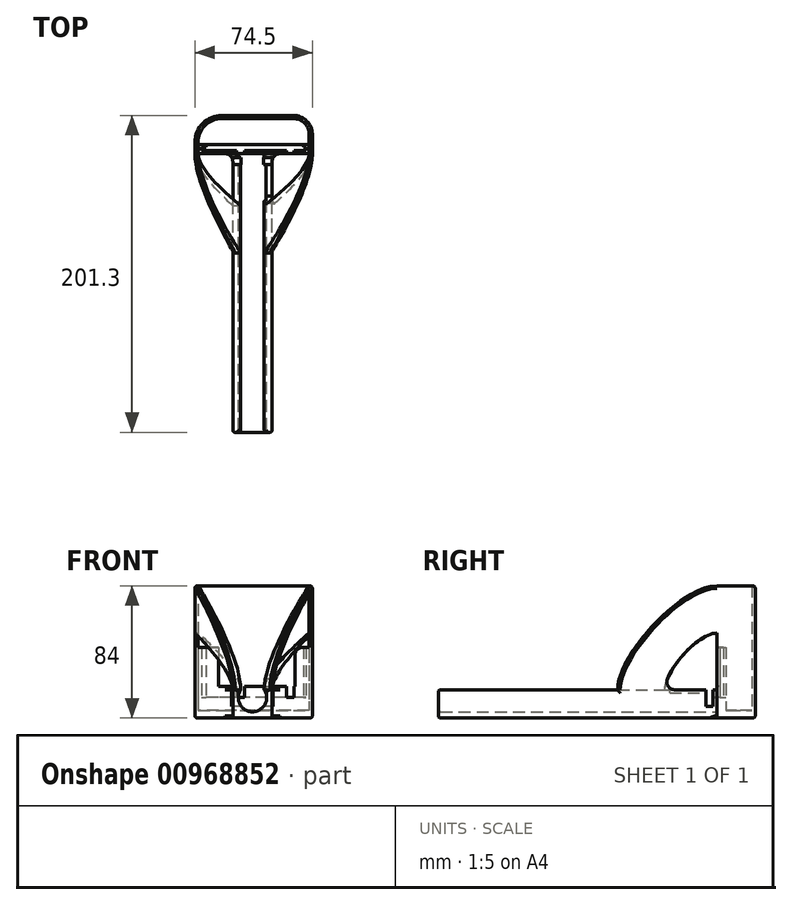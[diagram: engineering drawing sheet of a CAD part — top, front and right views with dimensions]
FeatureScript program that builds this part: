
annotation { "Feature Type Name" : "Feature", "Feature Type Description" : "" }
export const myFeature = defineFeature(function(context is Context, id is Id, definition is map)
    precondition{}
    {
        {
            var Q0;
            Q0=qCreatedBy(makeId("Top.planeOp"),FACE);
            var sketch = newSketch(context, id + "F0", { "sketchPlane" : qUnion([Q0])});
            skLineSegment(sketch, "E0.bottom", {"start": v(0, -2.2) * mm, "end": v(66.5, -2.2) * mm, "construction": true});
            skLineSegment(sketch, "E0.top", {"start": v(0, 0) * mm, "end": v(66.5, 0) * mm, "construction": true});
            skLineSegment(sketch, "E0.left", {"start": v(0, -2.2) * mm, "end": v(0, 0) * mm, "construction": true});
            skLineSegment(sketch, "E0.right", {"start": v(66.5, -2.2) * mm, "end": v(66.5, 0) * mm, "construction": true});
            skLineSegment(sketch, "E1", {"start": v(3, 0) * mm, "end": v(3, 1.6) * mm});
            skLineSegment(sketch, "E2", {"start": v(3, 1.6) * mm, "end": v(-2, 1.6) * mm});
            skLineSegment(sketch, "E3", {"start": v(-2, 1.6) * mm, "end": v(-2, -4.2) * mm});
            skLineSegment(sketch, "E4", {"start": v(-2, -4.2) * mm, "end": v(68.5, -4.2) * mm});
            skLineSegment(sketch, "E5", {"start": v(68.5, -4.2) * mm, "end": v(68.5, 1.6) * mm});
            skLineSegment(sketch, "E6", {"start": v(68.5, 1.6) * mm, "end": v(65, 1.6) * mm});
            skLineSegment(sketch, "E7", {"start": v(65, 1.6) * mm, "end": v(65, 0) * mm});
            skLineSegment(sketch, "E8", {"start": v(65, 0) * mm, "end": v(66.5, 0) * mm});
            skLineSegment(sketch, "E9", {"start": v(66.5, -2.2) * mm, "end": v(0, -2.2) * mm});
            skLineSegment(sketch, "E10", {"start": v(0, -2.2) * mm, "end": v(0, 0) * mm});
            skLineSegment(sketch, "E11", {"start": v(0, 0) * mm, "end": v(3, 0) * mm});
            skLineSegment(sketch, "E12", {"start": v(66.5, 0) * mm, "end": v(66.5, -2.2) * mm});
            skSolve(sketch);
        }
        {
            var Q0;
            Q0=makeQuery(id+"F0.imprint","IMPRINT",FACE,{"disambiguationData":[TD([[makeQuery(id+"F0.imprint","IMPRINT",EDGE,{"derivedFrom":sQuery(id+"F0.wireOp",EDGE,"E1")}),1.0]])]});
            extrude(context, id + "F1", {"entities" : qUnion([Q0]), "depth" : 45 * mm, "offsetDistance" : 25 * mm});
        }
        {
            var Q0;
            Q0=makeQuery(id+"F1.opExtrude","SWEPT_FACE",FACE,{"disambiguationData":[OSD([sQuery(id+"F0.wireOp",EDGE,"E4")])]});
            var sketch = newSketch(context, id + "F2", { "sketchPlane" : qUnion([Q0])});
            skLineSegment(sketch, "E13.0.0", {"start": v(-2, 0) * mm, "end": v(68.5, 0) * mm});
            skLineSegment(sketch, "E13.0.1", {"start": v(68.5, 0) * mm, "end": v(68.5, 45) * mm});
            skLineSegment(sketch, "E13.0.2", {"start": v(68.5, 45) * mm, "end": v(-2, 45) * mm});
            skLineSegment(sketch, "E13.0.3", {"start": v(-2, 45) * mm, "end": v(-2, 0) * mm});
            skLineSegment(sketch, "E14.0.1", {"start": v(0, 0) * mm, "end": v(0, 45) * mm});
            skLineSegment(sketch, "E14.0.3", {"start": v(0, 45) * mm, "end": v(0, 0) * mm});
            skLineSegment(sketch, "E15.0.1", {"start": v(66.5, 0) * mm, "end": v(66.5, 45) * mm});
            skLineSegment(sketch, "E15.0.3", {"start": v(66.5, 45) * mm, "end": v(66.5, 0) * mm});
            skLineSegment(sketch, "E16.bottom", {"start": v(11, 45) * mm, "end": v(59.5, 45) * mm});
            skLineSegment(sketch, "E16.top", {"start": v(11, 20) * mm, "end": v(59.5, 20) * mm});
            skLineSegment(sketch, "E16.left", {"start": v(11, 45) * mm, "end": v(11, 20) * mm});
            skLineSegment(sketch, "E16.right", {"start": v(59.5, 45) * mm, "end": v(59.5, 20) * mm});
            skSolve(sketch);
        }
        {
            var Q0;
            Q0=makeQuery(id+"F2.imprint","IMPRINT",FACE,{"disambiguationData":[TD([[makeQuery(id+"F2.imprint","IMPRINT",EDGE,{"derivedFrom":sQuery(id+"F2.wireOp",EDGE,"E16.top")}),1.0]])]});
            extrude(context, id + "F3", {"entities" : qUnion([Q0]), "operationType" : NewBodyOperationType.REMOVE, "oppositeDirection" : true, "depth" : 25 * mm, "offsetDistance" : 25 * mm});
        }
        {
            var Q0;
            Q0=makeQuery(id+"F1.opExtrude","SWEPT_FACE",FACE,{"disambiguationData":[OSD([sQuery(id+"F0.wireOp",EDGE,"E4")])]});
            var sketch = newSketch(context, id + "F4", { "sketchPlane" : qUnion([Q0])});
            skLineSegment(sketch, "E17.0.0", {"start": v(68.5, 45) * mm, "end": v(59.5, 45) * mm});
            skLineSegment(sketch, "E17.0.1", {"start": v(59.5, 45) * mm, "end": v(59.5, 20) * mm});
            skLineSegment(sketch, "E17.0.2", {"start": v(59.5, 20) * mm, "end": v(11, 20) * mm});
            skLineSegment(sketch, "E17.0.3", {"start": v(11, 20) * mm, "end": v(11, 45) * mm});
            skLineSegment(sketch, "E17.0.4", {"start": v(11, 45) * mm, "end": v(-2, 45) * mm});
            skLineSegment(sketch, "E17.0.5", {"start": v(-2, 45) * mm, "end": v(-2, 0) * mm});
            skLineSegment(sketch, "E17.0.6", {"start": v(-2, 0) * mm, "end": v(68.5, 0) * mm});
            skLineSegment(sketch, "E17.0.7", {"start": v(68.5, 0) * mm, "end": v(68.5, 45) * mm});
            skLineSegment(sketch, "E18.0.1", {"start": v(66.5, 0) * mm, "end": v(66.5, 45) * mm});
            skLineSegment(sketch, "E18.0.3", {"start": v(66.5, 45) * mm, "end": v(66.5, 0) * mm});
            skLineSegment(sketch, "E19.bottom", {"start": v(54, 20) * mm, "end": v(59, 20) * mm});
            skLineSegment(sketch, "E19.top", {"start": v(54, 13) * mm, "end": v(59, 13) * mm});
            skLineSegment(sketch, "E19.left", {"start": v(54, 20) * mm, "end": v(54, 13) * mm});
            skLineSegment(sketch, "E19.right", {"start": v(59, 20) * mm, "end": v(59, 13) * mm});
            skLineSegment(sketch, "E20.bottom", {"start": v(22.5, 20) * mm, "end": v(27.5, 20) * mm});
            skLineSegment(sketch, "E20.top", {"start": v(22.5, 13) * mm, "end": v(27.5, 13) * mm});
            skLineSegment(sketch, "E20.left", {"start": v(22.5, 20) * mm, "end": v(22.5, 13) * mm});
            skLineSegment(sketch, "E20.right", {"start": v(27.5, 20) * mm, "end": v(27.5, 13) * mm});
            skPoint(sketch, "E21", {"position": v(56.5, 20) * mm});
            skPoint(sketch, "E22", {"position": v(25, 20) * mm});
            skSolve(sketch);
        }
        {
            var Q0;
            Q0=makeQuery(id+"F4.imprint","IMPRINT",FACE,{"disambiguationData":[TD([[makeQuery(id+"F4.imprint","IMPRINT",EDGE,{"derivedFrom":sQuery(id+"F4.wireOp",EDGE,"E20.top")}),1.0]])]});
            var Q1;
            Q1=makeQuery(id+"F4.imprint","IMPRINT",FACE,{"disambiguationData":[TD([[makeQuery(id+"F4.imprint","IMPRINT",EDGE,{"derivedFrom":sQuery(id+"F4.wireOp",EDGE,"E19.top")}),1.0]])]});
            extrude(context, id + "F5", {"entities" : qUnion([Q0, Q1]), "operationType" : NewBodyOperationType.REMOVE, "oppositeDirection" : true, "depth" : 25 * mm, "offsetDistance" : 25 * mm});
        }
        {
            var Q0;
            Q0=makeQuery(id+"F1.opExtrude","SWEPT_FACE",FACE,{"disambiguationData":[OSD([sQuery(id+"F0.wireOp",EDGE,"E4")])]});
            var sketch = newSketch(context, id + "F6", { "sketchPlane" : qUnion([Q0])});
            skCircle(sketch, "E23", {"center": v(32.5, 13) * mm, "radius": 9 * mm, "construction": true});
            skLineSegment(sketch, "E24", {"start": v(20, 0) * mm, "end": v(20, 18) * mm});
            skLineSegment(sketch, "E25", {"start": v(20, 18) * mm, "end": v(25.02, 18) * mm});
            skLineSegment(sketch, "E26", {"start": v(45, 0) * mm, "end": v(45, 18) * mm});
            skLineSegment(sketch, "E27", {"start": v(45, 18) * mm, "end": v(39.98, 18) * mm});
            skArc(sketch, "E28", {"start": v(25.02, 18) * mm, "mid": v(32.5, 4) * mm, "end": v(39.98, 18) * mm});
            skLineSegment(sketch, "E29", {"start": v(20, 0) * mm, "end": v(45, 0) * mm});
            skPoint(sketch, "E30", {"position": v(32.5, 0) * mm});
            skPoint(sketch, "E30.positionSnap0", {"position": v(32.5, 0) * mm});
            skPoint(sketch, "E30.positionSnap1", {"position": v(32.5, 4) * mm});
            skSolve(sketch);
        }
        {
            var Q0;
            Q0=makeQuery(id+"F6.imprint","IMPRINT",FACE,{"disambiguationData":[TD([[makeQuery(id+"F6.imprint","IMPRINT",EDGE,{"derivedFrom":sQuery(id+"F6.wireOp",EDGE,"E24")}),-1.0]])]});
            var Q1;
            {var subQ0=sQuery(id+"F6.wireOp",EDGE,"E28");var subQ1=sQuery(id+"F6.wireOp",EDGE,"E25");var subQ2=makeQuery(id+"F6.imprint","INTERSECT",VERTEX,{"derivedFrom":[subQ1,subQ0]});Q1=makeQuery(id+"F6.imprint","IMPRINT",FACE,{"disambiguationData":[TD([[makeQuery(id+"F6.imprint","IMPRINT",EDGE,{"disambiguationData":[TD([[subQ2,1.0]])],"derivedFrom":subQ1}),-1.0]])]});}
            extrude(context, id + "F7", {"entities" : qUnion([Q0, Q1]), "operationType" : NewBodyOperationType.ADD, "depth" : 177 * mm, "offsetDistance" : 25 * mm});
        }
        {
            var Q0;
            Q0=makeQuery(id+"F7.opExtrude","SWEPT_FACE",FACE,{"disambiguationData":[OSD([sQuery(id+"F6.wireOp",EDGE,"E24")])]});
            var sketch = newSketch(context, id + "F8", { "sketchPlane" : qUnion([Q0])});
            skLineSegment(sketch, "E31.bottom", {"start": v(6.7, 22) * mm, "end": v(11.2, 22) * mm});
            skLineSegment(sketch, "E31.top", {"start": v(6.7, 7.5) * mm, "end": v(11.2, 7.5) * mm});
            skLineSegment(sketch, "E31.left", {"start": v(6.7, 22) * mm, "end": v(6.7, 7.5) * mm});
            skLineSegment(sketch, "E31.right", {"start": v(11.2, 22) * mm, "end": v(11.2, 7.5) * mm});
            skLineSegment(sketch, "E32.0.1", {"start": v(4.2, 0) * mm, "end": v(4.2, 18) * mm});
            skLineSegment(sketch, "E32.0.3", {"start": v(4.2, 18) * mm, "end": v(4.2, 18) * mm});
            skLineSegment(sketch, "E32.0.5", {"start": v(4.2, 18) * mm, "end": v(4.2, 0) * mm});
            skLineSegment(sketch, "E32.0.7", {"start": v(4.2, 0) * mm, "end": v(4.2, 45) * mm});
            skLineSegment(sketch, "E32.0.9", {"start": v(4.2, 45) * mm, "end": v(4.2, 20) * mm});
            skLineSegment(sketch, "E32.0.11", {"start": v(4.2, 20) * mm, "end": v(4.2, 13) * mm});
            skLineSegment(sketch, "E32.0.13", {"start": v(4.2, 13) * mm, "end": v(4.2, 20) * mm});
            skLineSegment(sketch, "E32.0.15", {"start": v(4.2, 20) * mm, "end": v(4.2, 13) * mm});
            skLineSegment(sketch, "E32.0.17", {"start": v(4.2, 18) * mm, "end": v(4.2, 20) * mm});
            skLineSegment(sketch, "E32.0.19", {"start": v(4.2, 20) * mm, "end": v(4.2, 45) * mm});
            skLineSegment(sketch, "E32.0.21", {"start": v(4.2, 45) * mm, "end": v(4.2, 0) * mm});
            skSolve(sketch);
        }
        {
            var Q0;
            {var subQ0=sQuery(id+"F8.wireOp",EDGE,"E31.top");Q0=makeQuery(id+"F8.imprint","IMPRINT",FACE,{"disambiguationData":[TD([[makeQuery(id+"F8.imprint","IMPRINT",EDGE,{"derivedFrom":subQ0}),1.0]])]});}
            var Q1;
            {var subQ0=sQuery(id+"F8.wireOp",EDGE,"E31.bottom");Q1=makeQuery(id+"F8.imprint","IMPRINT",FACE,{"disambiguationData":[TD([[makeQuery(id+"F8.imprint","IMPRINT",EDGE,{"derivedFrom":subQ0}),-1.0]])]});}
            extrude(context, id + "F9", {"entities" : qUnion([Q0, Q1]), "operationType" : NewBodyOperationType.REMOVE, "oppositeDirection" : true, "depth" : 25 * mm, "offsetDistance" : 25 * mm});
        }
        {
            var Q0;
            Q0=makeQuery(id+"F7.boolean.opBoolean","MERGE",FACE,{"derivedFrom":[makeQuery(id+"F1.opExtrude","CAP_FACE",FACE,{"disambiguationData":[OSD([sQuery(id+"F0.wireOp",EDGE,"E1"),sQuery(id+"F0.wireOp",EDGE,"E2"),sQuery(id+"F0.wireOp",EDGE,"E3"),sQuery(id+"F0.wireOp",EDGE,"E4"),sQuery(id+"F0.wireOp",EDGE,"E5"),sQuery(id+"F0.wireOp",EDGE,"E6"),sQuery(id+"F0.wireOp",EDGE,"E7"),sQuery(id+"F0.wireOp",EDGE,"E8"),sQuery(id+"F0.wireOp",EDGE,"E9"),sQuery(id+"F0.wireOp",EDGE,"E10"),sQuery(id+"F0.wireOp",EDGE,"E11"),sQuery(id+"F0.wireOp",EDGE,"E12")])],"isStart":true}),makeQuery(id+"F7.opExtrude","SWEPT_FACE",FACE,{"disambiguationData":[OSD([sQuery(id+"F6.wireOp",EDGE,"E29")])]})]});
            var sketch = newSketch(context, id + "F10", { "sketchPlane" : qUnion([Q0])});
            skLineSegment(sketch, "E33.0.0", {"start": v(0, 2.2) * mm, "end": v(66.5, 2.2) * mm});
            skLineSegment(sketch, "E33.0.1", {"start": v(66.5, 2.2) * mm, "end": v(66.5, 0) * mm});
            skLineSegment(sketch, "E33.0.2", {"start": v(66.5, 0) * mm, "end": v(65, 0) * mm});
            skLineSegment(sketch, "E33.0.3", {"start": v(65, 0) * mm, "end": v(65, -1.6) * mm});
            skLineSegment(sketch, "E33.0.4", {"start": v(65, -1.6) * mm, "end": v(68.5, -1.6) * mm});
            skLineSegment(sketch, "E33.0.5", {"start": v(68.5, -1.6) * mm, "end": v(68.5, 4.2) * mm});
            skLineSegment(sketch, "E33.0.6", {"start": v(68.5, 4.2) * mm, "end": v(45, 4.2) * mm});
            skLineSegment(sketch, "E33.0.7", {"start": v(45, 4.2) * mm, "end": v(45, 181.2) * mm});
            skLineSegment(sketch, "E33.0.8", {"start": v(45, 181.2) * mm, "end": v(20, 181.2) * mm});
            skLineSegment(sketch, "E33.0.9", {"start": v(20, 181.2) * mm, "end": v(20, 4.2) * mm});
            skLineSegment(sketch, "E33.0.10", {"start": v(20, 4.2) * mm, "end": v(-2, 4.2) * mm});
            skLineSegment(sketch, "E33.0.11", {"start": v(-2, 4.2) * mm, "end": v(-2, -1.6) * mm});
            skLineSegment(sketch, "E33.0.12", {"start": v(-2, -1.6) * mm, "end": v(3, -1.6) * mm});
            skLineSegment(sketch, "E33.0.13", {"start": v(3, -1.6) * mm, "end": v(3, 0) * mm});
            skLineSegment(sketch, "E33.0.14", {"start": v(3, 0) * mm, "end": v(0, 0) * mm});
            skLineSegment(sketch, "E33.0.15", {"start": v(0, 0) * mm, "end": v(0, 2.2) * mm});
            skLineSegment(sketch, "E34", {"start": v(65, -1.6) * mm, "end": v(3, -1.6) * mm});
            skSolve(sketch);
        }
        {
            var Q0;
            Q0=makeQuery(id+"F10.imprint","IMPRINT",FACE,{"disambiguationData":[TD([[makeQuery(id+"F10.imprint","IMPRINT",EDGE,{"derivedFrom":sQuery(id+"F10.wireOp",EDGE,"E33.0.0")}),1.0]])]});
            extrude(context, id + "F11", {"entities" : qUnion([Q0]), "operationType" : NewBodyOperationType.ADD, "oppositeDirection" : true, "depth" : 13 * mm, "offsetDistance" : 25 * mm});
        }
        {
            var Q0;
            Q0=makeQuery(id+"F11.boolean.opBoolean","MERGE",FACE,{"derivedFrom":[makeQuery(id+"F7.boolean.opBoolean","MERGE",FACE,{"derivedFrom":[makeQuery(id+"F1.opExtrude","CAP_FACE",FACE,{"disambiguationData":[OSD([sQuery(id+"F0.wireOp",EDGE,"E1"),sQuery(id+"F0.wireOp",EDGE,"E2"),sQuery(id+"F0.wireOp",EDGE,"E3"),sQuery(id+"F0.wireOp",EDGE,"E4"),sQuery(id+"F0.wireOp",EDGE,"E5"),sQuery(id+"F0.wireOp",EDGE,"E6"),sQuery(id+"F0.wireOp",EDGE,"E7"),sQuery(id+"F0.wireOp",EDGE,"E8"),sQuery(id+"F0.wireOp",EDGE,"E9"),sQuery(id+"F0.wireOp",EDGE,"E10"),sQuery(id+"F0.wireOp",EDGE,"E11"),sQuery(id+"F0.wireOp",EDGE,"E12")])],"isStart":true}),makeQuery(id+"F7.opExtrude","SWEPT_FACE",FACE,{"disambiguationData":[OSD([sQuery(id+"F6.wireOp",EDGE,"E29")])]})]}),makeQuery(id+"F11.opExtrude","CAP_FACE",FACE,{"disambiguationData":[OSD([sQuery(id+"F10.wireOp",EDGE,"E33.0.0"),sQuery(id+"F10.wireOp",EDGE,"E33.0.1"),sQuery(id+"F10.wireOp",EDGE,"E33.0.2"),sQuery(id+"F10.wireOp",EDGE,"E33.0.3"),sQuery(id+"F10.wireOp",EDGE,"E33.0.13"),sQuery(id+"F10.wireOp",EDGE,"E33.0.14"),sQuery(id+"F10.wireOp",EDGE,"E33.0.15"),sQuery(id+"F10.wireOp",EDGE,"E34")])],"isStart":true})]});
            var sketch = newSketch(context, id + "F12", { "sketchPlane" : qUnion([Q0])});
            skLineSegment(sketch, "E35.0.0", {"start": v(-2, 4.2) * mm, "end": v(-2, -1.6) * mm});
            skLineSegment(sketch, "E35.0.1", {"start": v(-2, -1.6) * mm, "end": v(68.5, -1.6) * mm});
            skLineSegment(sketch, "E35.0.2", {"start": v(68.5, -1.6) * mm, "end": v(68.5, 4.2) * mm});
            skLineSegment(sketch, "E35.0.3", {"start": v(68.5, 4.2) * mm, "end": v(45, 4.2) * mm});
            skLineSegment(sketch, "E35.0.4", {"start": v(45, 4.2) * mm, "end": v(45, 181.2) * mm});
            skLineSegment(sketch, "E35.0.5", {"start": v(45, 181.2) * mm, "end": v(20, 181.2) * mm});
            skLineSegment(sketch, "E35.0.6", {"start": v(20, 181.2) * mm, "end": v(20, 4.2) * mm});
            skLineSegment(sketch, "E35.0.7", {"start": v(20, 4.2) * mm, "end": v(-2, 4.2) * mm});
            skLineSegment(sketch, "E36", {"start": v(68.5, 4.2) * mm, "end": v(70.5, 4.2) * mm});
            skLineSegment(sketch, "E37", {"start": v(70.5, 4.2) * mm, "end": v(70.5, -8.1) * mm});
            skLineSegment(sketch, "E38", {"start": v(58.5, -20.1) * mm, "end": v(13, -20.1) * mm});
            skLineSegment(sketch, "E39", {"start": v(-4, -3.1) * mm, "end": v(-4, 4.2) * mm});
            skLineSegment(sketch, "E40", {"start": v(-4, 4.2) * mm, "end": v(-2, 4.2) * mm});
            skLineSegment(sketch, "E41", {"start": v(-2, -1.6) * mm, "end": v(-2, -3.1) * mm});
            skLineSegment(sketch, "E42", {"start": v(13, -18.1) * mm, "end": v(58.5, -18.1) * mm});
            skLineSegment(sketch, "E43", {"start": v(68.5, -8.1) * mm, "end": v(68.5, -1.6) * mm});
            skPoint(sketch, "E44.visualSharp", {"position": v(68.5, -18.1) * mm});
            skArc(sketch, "E44.filletArc", {"start": v(58.5, -18.1) * mm, "mid": v(65.57, -15.17) * mm, "end": v(68.5, -8.1) * mm});
            skPoint(sketch, "E45.visualSharp", {"position": v(-2, -18.1) * mm});
            skArc(sketch, "E45.filletArc", {"start": v(-2, -3.1) * mm, "mid": v(2.4, -13.7) * mm, "end": v(13, -18.1) * mm});
            skPoint(sketch, "E46.visualSharp", {"position": v(-4, -20.1) * mm});
            skArc(sketch, "E46.filletArc", {"start": v(-4, -3.1) * mm, "mid": v(0.98, -15.12) * mm, "end": v(13, -20.1) * mm});
            skPoint(sketch, "E47.visualSharp", {"position": v(70.5, -20.1) * mm});
            skArc(sketch, "E47.filletArc", {"start": v(58.5, -20.1) * mm, "mid": v(66.99, -16.59) * mm, "end": v(70.5, -8.1) * mm});
            skSolve(sketch);
        }
        {
            var Q0;
            Q0=makeQuery(id+"F12.imprint","IMPRINT",FACE,{"disambiguationData":[TD([[makeQuery(id+"F12.imprint","IMPRINT",EDGE,{"derivedFrom":sQuery(id+"F12.wireOp",EDGE,"E35.0.0")}),1.0]])]});
            extrude(context, id + "F13", {"entities" : qUnion([Q0]), "operationType" : NewBodyOperationType.ADD, "oppositeDirection" : true, "depth" : 84 * mm, "offsetDistance" : 25 * mm});
        }
        {
            var Q0;
            {var subQ1=sQuery(id+"F6.wireOp",EDGE,"E27");Q0=makeQuery(id+"F9.boolean.opBoolean","SPLIT",FACE,{"disambiguationData":[TD([makeQuery(id+"F9.opExtrude","SWEPT_FACE",FACE,{"disambiguationData":[OSD([sQuery(id+"F8.wireOp",EDGE,"E31.right")])]})])],"derivedFrom":makeQuery(id+"F7.opExtrude","SWEPT_FACE",FACE,{"disambiguationData":[OSD([subQ1])]})});}
            var sketch = newSketch(context, id + "F14", { "sketchPlane" : qUnion([Q0])});
            skLineSegment(sketch, "E48.bottom", {"start": v(39.98, -11.2) * mm, "end": v(40.98, -11.2) * mm});
            skLineSegment(sketch, "E48.top", {"start": v(39.98, -34.2) * mm, "end": v(40.98, -34.2) * mm});
            skLineSegment(sketch, "E48.left", {"start": v(39.98, -11.2) * mm, "end": v(39.98, -34.2) * mm});
            skLineSegment(sketch, "E48.right", {"start": v(40.98, -11.2) * mm, "end": v(40.98, -34.2) * mm});
            skSolve(sketch);
        }
        {
            var Q0;
            Q0=makeQuery(id+"F14.imprint","IMPRINT",FACE,{"disambiguationData":[TD([[makeQuery(id+"F14.imprint","IMPRINT",EDGE,{"derivedFrom":sQuery(id+"F14.wireOp",EDGE,"E48.bottom")}),-1.0]])]});
            var Q1;
            {var subQ2=sQuery(id+"F4.wireOp",EDGE,"E20.top");Q1=makeQuery(id+"F9.boolean.opBoolean","SPLIT",FACE,{"disambiguationData":[TD([makeQuery(id+"F9.opExtrude","SWEPT_FACE",FACE,{"disambiguationData":[OSD([sQuery(id+"F8.wireOp",EDGE,"E31.right")])]})])],"derivedFrom":makeQuery(id+"F7.boolean.opBoolean","MERGE",FACE,{"derivedFrom":[makeQuery(id+"F5.boolean.opBoolean","COPY",FACE,{"derivedFrom":makeQuery(id+"F5.opExtrude","SWEPT_FACE",FACE,{"disambiguationData":[OSD([subQ2])]})}),makeQuery(id+"F7.opExtrude","SWEPT_FACE",FACE,{"disambiguationData":[OSD([subQ2])]})]})});}
            extrude(context, id + "F15", {"entities" : qUnion([Q0]), "operationType" : NewBodyOperationType.REMOVE, "oppositeDirection" : true, "depth" : 5 * mm, "endBoundEntityFace" : qUnion([Q1]), "offsetDistance" : 25 * mm});
        }
        {
            var Q0;
            {var subQ0=sQuery(id+"F0.wireOp",EDGE,"E3");var subQ9=sQuery(id+"F0.wireOp",EDGE,"E4");Q0=makeQuery(id+"F13.boolean.opBoolean","MERGE",FACE,{"derivedFrom":[makeQuery(id+"F7.boolean.opBoolean","SPLIT",FACE,{"disambiguationData":[TD([makeQuery(id+"F1.opExtrude","SWEPT_FACE",FACE,{"disambiguationData":[OSD([subQ0])]})])],"derivedFrom":makeQuery(id+"F1.opExtrude","SWEPT_FACE",FACE,{"disambiguationData":[OSD([subQ9])]})}),makeQuery(id+"F13.opExtrude","SWEPT_FACE",FACE,{"disambiguationData":[OSD([sQuery(id+"F12.wireOp",EDGE,"E40")])]})]});}
            var sketch = newSketch(context, id + "F16", { "sketchPlane" : qUnion([Q0])});
            skLineSegment(sketch, "E49.bottom", {"start": v(-4, 84) * mm, "end": v(-2, 84) * mm});
            skLineSegment(sketch, "E49.top", {"start": v(-4, 54) * mm, "end": v(-2, 54) * mm});
            skLineSegment(sketch, "E49.left", {"start": v(-4, 84) * mm, "end": v(-4, 54) * mm});
            skLineSegment(sketch, "E49.right", {"start": v(-2, 84) * mm, "end": v(-2, 54) * mm});
            skSolve(sketch);
        }
        {
            var Q0;
            {var subQ1=sQuery(id+"F6.wireOp",EDGE,"E25");Q0=makeQuery(id+"F9.boolean.opBoolean","SPLIT",FACE,{"disambiguationData":[TD([makeQuery(id+"F9.opExtrude","SWEPT_FACE",FACE,{"disambiguationData":[OSD([sQuery(id+"F8.wireOp",EDGE,"E31.right")])]})])],"derivedFrom":makeQuery(id+"F7.opExtrude","SWEPT_FACE",FACE,{"disambiguationData":[OSD([subQ1])]})});}
            var sketch = newSketch(context, id + "F17", { "sketchPlane" : qUnion([Q0])});
            skLineSegment(sketch, "E50.bottom", {"start": v(20, -37.2) * mm, "end": v(20, -37.2) * mm});
            skLineSegment(sketch, "E50.top", {"start": v(20, -67.2) * mm, "end": v(20, -67.2) * mm});
            skLineSegment(sketch, "E50.left", {"start": v(20, -37.2) * mm, "end": v(20, -67.2) * mm});
            skLineSegment(sketch, "E50.right", {"start": v(20, -37.2) * mm, "end": v(20, -67.2) * mm});
            skLineSegment(sketch, "E51.bottom", {"start": v(20, -37.2) * mm, "end": v(25.02, -37.2) * mm});
            skLineSegment(sketch, "E51.top", {"start": v(20, -67.2) * mm, "end": v(25.02, -67.2) * mm});
            skLineSegment(sketch, "E51.right", {"start": v(25.02, -37.2) * mm, "end": v(25.02, -67.2) * mm});
            skSolve(sketch);
        }
        {
            var Q1;
            Q1=makeQuery(id+"F17.imprint","IMPRINT",FACE,{"disambiguationData":[TD([[makeQuery(id+"F17.imprint","IMPRINT",EDGE,{"derivedFrom":sQuery(id+"F17.wireOp",EDGE,"E51.bottom")}),-1.0]])]});
            var Q2;
            Q2=makeQuery(id+"F16.imprint","IMPRINT",FACE,{"disambiguationData":[TD([[makeQuery(id+"F16.imprint","IMPRINT",EDGE,{"derivedFrom":sQuery(id+"F16.wireOp",EDGE,"E49.bottom")}),-1.0]])]});
            loft(context, id + "F18", {"operationType" : NewBodyOperationType.ADD, "startCondition" : LoftEndDerivativeType.NORMAL_TO_PROFILE, "startMagnitude" : 1, "endCondition" : LoftEndDerivativeType.NORMAL_TO_PROFILE, "endMagnitude" : 1, "sheetProfilesArray" : [{ "sheetProfileEntities" : qUnion([Q1]) }, { "sheetProfileEntities" : qUnion([Q2]) }]});
        }
        {
            var Q0;
            {var subQ8=sQuery(id+"F0.wireOp",EDGE,"E5");var subQ9=sQuery(id+"F0.wireOp",EDGE,"E4");Q0=makeQuery(id+"F13.boolean.opBoolean","MERGE",FACE,{"derivedFrom":[makeQuery(id+"F7.boolean.opBoolean","SPLIT",FACE,{"disambiguationData":[TD([makeQuery(id+"F1.opExtrude","SWEPT_FACE",FACE,{"disambiguationData":[OSD([subQ8])]})])],"derivedFrom":makeQuery(id+"F1.opExtrude","SWEPT_FACE",FACE,{"disambiguationData":[OSD([subQ9])]})}),makeQuery(id+"F13.opExtrude","SWEPT_FACE",FACE,{"disambiguationData":[OSD([sQuery(id+"F12.wireOp",EDGE,"E36")])]})]});}
            var sketch = newSketch(context, id + "F19", { "sketchPlane" : qUnion([Q0])});
            skLineSegment(sketch, "E52.bottom", {"start": v(68.5, 84) * mm, "end": v(70.5, 84) * mm});
            skLineSegment(sketch, "E52.top", {"start": v(68.5, 54) * mm, "end": v(70.5, 54) * mm});
            skLineSegment(sketch, "E52.left", {"start": v(68.5, 84) * mm, "end": v(68.5, 54) * mm});
            skLineSegment(sketch, "E52.right", {"start": v(70.5, 84) * mm, "end": v(70.5, 54) * mm});
            skSolve(sketch);
        }
        {
            var Q0;
            {var subQ1=sQuery(id+"F6.wireOp",EDGE,"E27");Q0=makeQuery(id+"F9.boolean.opBoolean","SPLIT",FACE,{"disambiguationData":[TD([makeQuery(id+"F9.opExtrude","SWEPT_FACE",FACE,{"disambiguationData":[OSD([sQuery(id+"F8.wireOp",EDGE,"E31.right")])]})])],"derivedFrom":makeQuery(id+"F7.opExtrude","SWEPT_FACE",FACE,{"disambiguationData":[OSD([subQ1])]})});}
            var sketch = newSketch(context, id + "F20", { "sketchPlane" : qUnion([Q0])});
            skLineSegment(sketch, "E53.bottom", {"start": v(39.98, -37.2) * mm, "end": v(45, -37.2) * mm});
            skLineSegment(sketch, "E53.top", {"start": v(39.98, -67.2) * mm, "end": v(45, -67.2) * mm});
            skLineSegment(sketch, "E53.left", {"start": v(39.98, -37.2) * mm, "end": v(39.98, -67.2) * mm});
            skLineSegment(sketch, "E53.right", {"start": v(45, -37.2) * mm, "end": v(45, -67.2) * mm});
            skSolve(sketch);
        }
        {
            var Q1;
            Q1=makeQuery(id+"F19.imprint","IMPRINT",FACE,{"disambiguationData":[TD([[makeQuery(id+"F19.imprint","IMPRINT",EDGE,{"derivedFrom":sQuery(id+"F19.wireOp",EDGE,"E52.bottom")}),-1.0]])]});
            var Q2;
            Q2=makeQuery(id+"F20.imprint","IMPRINT",FACE,{"disambiguationData":[TD([[makeQuery(id+"F20.imprint","IMPRINT",EDGE,{"derivedFrom":sQuery(id+"F20.wireOp",EDGE,"E53.bottom")}),-1.0]])]});
            loft(context, id + "F21", {"operationType" : NewBodyOperationType.ADD, "startCondition" : LoftEndDerivativeType.NORMAL_TO_PROFILE, "startMagnitude" : 1, "endCondition" : LoftEndDerivativeType.NORMAL_TO_PROFILE, "endMagnitude" : 1, "sheetProfilesArray" : [{ "sheetProfileEntities" : qUnion([Q1]) }, { "sheetProfileEntities" : qUnion([Q2]) }]});
        }
        {
            var Q0;
            Q0=makeQuery(id+"F7.opExtrude","CAP_FACE",FACE,{"disambiguationData":[OSD([sQuery(id+"F6.wireOp",EDGE,"E24"),sQuery(id+"F6.wireOp",EDGE,"E25"),sQuery(id+"F6.wireOp",EDGE,"E26"),sQuery(id+"F6.wireOp",EDGE,"E27"),sQuery(id+"F6.wireOp",EDGE,"E28"),sQuery(id+"F6.wireOp",EDGE,"E29")])],"isStart":false});
            fillet(context, id + "F22", {"entities" : qUnion([Q0]), "radius" : 1.5 * mm, "tangentPropagation" : true, "allowEdgeOverflow" : false});
        }
        {
            var Q0;
            Q0=makeQuery(id+"F22.opFillet","BLEND_EDGE",EDGE,{"blendedFrom":[makeQuery(id+"F7.opExtrude","CAP_EDGE",EDGE,{"disambiguationData":[OSD([sQuery(id+"F6.wireOp",EDGE,"E26")])],"isStart":false}),makeQuery(id+"F7.opExtrude","CAP_EDGE",EDGE,{"disambiguationData":[OSD([sQuery(id+"F6.wireOp",EDGE,"E29")])],"isStart":false})],"blendedInto":[]});
            var Q1;
            Q1=makeQuery(id+"F22.opFillet","BLEND_EDGE",EDGE,{"blendedFrom":[makeQuery(id+"F7.opExtrude","CAP_EDGE",EDGE,{"disambiguationData":[OSD([sQuery(id+"F6.wireOp",EDGE,"E24")])],"isStart":false}),makeQuery(id+"F7.opExtrude","CAP_EDGE",EDGE,{"disambiguationData":[OSD([sQuery(id+"F6.wireOp",EDGE,"E29")])],"isStart":false})],"blendedInto":[]});
            var Q2;
            Q2=makeQuery(id+"F22.opFillet","BLEND_EDGE",EDGE,{"blendedFrom":[makeQuery(id+"F7.opExtrude","CAP_EDGE",EDGE,{"disambiguationData":[OSD([sQuery(id+"F6.wireOp",EDGE,"E26")])],"isStart":false}),makeQuery(id+"F7.opExtrude","CAP_EDGE",EDGE,{"disambiguationData":[OSD([sQuery(id+"F6.wireOp",EDGE,"E27")])],"isStart":false})],"blendedInto":[]});
            var Q3;
            Q3=makeQuery(id+"F22.opFillet","BLEND_EDGE",EDGE,{"blendedFrom":[makeQuery(id+"F7.opExtrude","CAP_EDGE",EDGE,{"disambiguationData":[OSD([sQuery(id+"F6.wireOp",EDGE,"E24")])],"isStart":false}),makeQuery(id+"F7.opExtrude","CAP_EDGE",EDGE,{"disambiguationData":[OSD([sQuery(id+"F6.wireOp",EDGE,"E25")])],"isStart":false})],"blendedInto":[]});
            fillet(context, id + "F23", {"entities" : qUnion([Q0, Q1, Q2, Q3]), "radius" : 2 * mm, "tangentPropagation" : true, "allowEdgeOverflow" : false});
        }
        {
            var Q0;
            Q0=makeQuery(id+"F7.opExtrude","CAP_EDGE",EDGE,{"disambiguationData":[OSD([sQuery(id+"F6.wireOp",EDGE,"E26")])],"isStart":true});
            var Q1;
            {var subQ8=sQuery(id+"F0.wireOp",EDGE,"E5");var subQ9=sQuery(id+"F0.wireOp",EDGE,"E4");var subQ13=sQuery(id+"F6.wireOp",EDGE,"E26");var subQ14=sQuery(id+"F6.wireOp",EDGE,"E29");Q1=makeQuery(id+"F23.opFillet","BLEND_EDGE",EDGE,{"blendedFrom":[makeQuery(id+"F7.opExtrude","SWEPT_EDGE",EDGE,{"disambiguationData":[OSD([subQ9,subQ13,subQ14])]}),makeQuery(id+"F13.boolean.opBoolean","MERGE",FACE,{"derivedFrom":[makeQuery(id+"F7.boolean.opBoolean","SPLIT",FACE,{"disambiguationData":[TD([makeQuery(id+"F1.opExtrude","SWEPT_FACE",FACE,{"disambiguationData":[OSD([subQ8])]})])],"derivedFrom":makeQuery(id+"F1.opExtrude","SWEPT_FACE",FACE,{"disambiguationData":[OSD([subQ9])]})}),makeQuery(id+"F13.opExtrude","SWEPT_FACE",FACE,{"disambiguationData":[OSD([sQuery(id+"F12.wireOp",EDGE,"E36")])]})]})],"blendedInto":[makeQuery(id+"F13.boolean.opBoolean","MERGE",FACE,{"derivedFrom":[makeQuery(id+"F7.boolean.opBoolean","SPLIT",FACE,{"disambiguationData":[TD([makeQuery(id+"F1.opExtrude","SWEPT_FACE",FACE,{"disambiguationData":[OSD([subQ8])]})])],"derivedFrom":makeQuery(id+"F1.opExtrude","SWEPT_FACE",FACE,{"disambiguationData":[OSD([subQ9])]})}),makeQuery(id+"F13.opExtrude","SWEPT_FACE",FACE,{"disambiguationData":[OSD([sQuery(id+"F12.wireOp",EDGE,"E36")])]})]})]});}
            var Q2;
            Q2=makeQuery(id+"F7.opExtrude","CAP_EDGE",EDGE,{"disambiguationData":[OSD([sQuery(id+"F6.wireOp",EDGE,"E24")])],"isStart":true});
            var Q3;
            {var subQ0=sQuery(id+"F0.wireOp",EDGE,"E3");var subQ9=sQuery(id+"F0.wireOp",EDGE,"E4");var subQ13=sQuery(id+"F6.wireOp",EDGE,"E24");var subQ14=sQuery(id+"F6.wireOp",EDGE,"E29");Q3=makeQuery(id+"F23.opFillet","BLEND_EDGE",EDGE,{"blendedFrom":[makeQuery(id+"F7.opExtrude","SWEPT_EDGE",EDGE,{"disambiguationData":[OSD([subQ9,subQ13,subQ14])]}),makeQuery(id+"F13.boolean.opBoolean","MERGE",FACE,{"derivedFrom":[makeQuery(id+"F7.boolean.opBoolean","SPLIT",FACE,{"disambiguationData":[TD([makeQuery(id+"F1.opExtrude","SWEPT_FACE",FACE,{"disambiguationData":[OSD([subQ0])]})])],"derivedFrom":makeQuery(id+"F1.opExtrude","SWEPT_FACE",FACE,{"disambiguationData":[OSD([subQ9])]})}),makeQuery(id+"F13.opExtrude","SWEPT_FACE",FACE,{"disambiguationData":[OSD([sQuery(id+"F12.wireOp",EDGE,"E40")])]})]})],"blendedInto":[makeQuery(id+"F13.boolean.opBoolean","MERGE",FACE,{"derivedFrom":[makeQuery(id+"F7.boolean.opBoolean","SPLIT",FACE,{"disambiguationData":[TD([makeQuery(id+"F1.opExtrude","SWEPT_FACE",FACE,{"disambiguationData":[OSD([subQ0])]})])],"derivedFrom":makeQuery(id+"F1.opExtrude","SWEPT_FACE",FACE,{"disambiguationData":[OSD([subQ9])]})}),makeQuery(id+"F13.opExtrude","SWEPT_FACE",FACE,{"disambiguationData":[OSD([sQuery(id+"F12.wireOp",EDGE,"E40")])]})]})]});}
            fillet(context, id + "F24", {"entities" : qUnion([Q0, Q1, Q2, Q3]), "radius" : 5 * mm, "tangentPropagation" : true, "allowEdgeOverflow" : false});
        }
        {
            var Q0;
            {var subQ0=sQuery(id+"F0.wireOp",EDGE,"E4");var subQ1=sQuery(id+"F0.wireOp",EDGE,"E5");Q0=makeQuery(id+"F13.boolean.opBoolean","MERGE",EDGE,{"derivedFrom":[makeQuery(id+"F7.boolean.opBoolean","SPLIT",EDGE,{"disambiguationData":[TD([makeQuery(id+"F1.opExtrude","SWEPT_FACE",FACE,{"disambiguationData":[OSD([subQ1])]})])],"derivedFrom":makeQuery(id+"F1.opExtrude","CAP_EDGE",EDGE,{"disambiguationData":[OSD([subQ0])],"isStart":true})}),makeQuery(id+"F13.opExtrude","CAP_EDGE",EDGE,{"disambiguationData":[OSD([sQuery(id+"F12.wireOp",EDGE,"E36")])],"isStart":true})]});}
            var Q1;
            Q1=makeQuery(id+"F13.opExtrude","CAP_EDGE",EDGE,{"disambiguationData":[OSD([sQuery(id+"F12.wireOp",EDGE,"E37")])],"isStart":true});
            var Q2;
            Q2=makeQuery(id+"F13.opExtrude","CAP_EDGE",EDGE,{"disambiguationData":[OSD([sQuery(id+"F12.wireOp",EDGE,"E38")])],"isStart":true});
            var Q3;
            Q3=makeQuery(id+"F13.opExtrude","CAP_EDGE",EDGE,{"disambiguationData":[OSD([sQuery(id+"F12.wireOp",EDGE,"E39")])],"isStart":true});
            var Q4;
            {var subQ0=sQuery(id+"F0.wireOp",EDGE,"E4");var subQ1=sQuery(id+"F0.wireOp",EDGE,"E3");Q4=makeQuery(id+"F13.boolean.opBoolean","MERGE",EDGE,{"derivedFrom":[makeQuery(id+"F7.boolean.opBoolean","SPLIT",EDGE,{"disambiguationData":[TD([makeQuery(id+"F1.opExtrude","SWEPT_FACE",FACE,{"disambiguationData":[OSD([subQ1])]})])],"derivedFrom":makeQuery(id+"F1.opExtrude","CAP_EDGE",EDGE,{"disambiguationData":[OSD([subQ0])],"isStart":true})}),makeQuery(id+"F13.opExtrude","CAP_EDGE",EDGE,{"disambiguationData":[OSD([sQuery(id+"F12.wireOp",EDGE,"E40")])],"isStart":true})]});}
            fillet(context, id + "F25", {"entities" : qUnion([Q0, Q1, Q2, Q3, Q4]), "radius" : 1.5 * mm, "tangentPropagation" : true, "allowEdgeOverflow" : false});
        }
        {
            var Q0;
            Q0=makeQuery(id+"F13.opExtrude","CAP_EDGE",EDGE,{"disambiguationData":[OSD([sQuery(id+"F12.wireOp",EDGE,"E37")])],"isStart":false});
            var Q1;
            Q1=makeQuery(id+"F13.opExtrude","CAP_EDGE",EDGE,{"disambiguationData":[OSD([sQuery(id+"F12.wireOp",EDGE,"E38")])],"isStart":false});
            var Q2;
            Q2=makeQuery(id+"F13.opExtrude","CAP_EDGE",EDGE,{"disambiguationData":[OSD([sQuery(id+"F12.wireOp",EDGE,"E39")])],"isStart":false});
            fillet(context, id + "F26", {"entities" : qUnion([Q0, Q1, Q2]), "radius" : 1.5 * mm, "tangentPropagation" : true, "allowEdgeOverflow" : false});
        }
        {
            var Q0;
            Q0=makeQuery(id+"F21.opLoft","MID_CAP_EDGE",EDGE,{"disambiguationData":[OSD([sQuery(id+"F6.wireOp",EDGE,"E26"),sQuery(id+"F6.wireOp",EDGE,"E27"),sQuery(id+"F6.wireOp",EDGE,"E28"),sQuery(id+"F20.wireOp",EDGE,"E53.top"),sQuery(id+"F20.wireOp",EDGE,"E53.left"),sQuery(id+"F20.wireOp",EDGE,"E53.right")])],"capPos":1.0});
            var Q1;
            Q1=makeQuery(id+"F18.opLoft","MID_CAP_EDGE",EDGE,{"disambiguationData":[OSD([sQuery(id+"F4.wireOp",EDGE,"E20.left"),sQuery(id+"F6.wireOp",EDGE,"E24"),sQuery(id+"F6.wireOp",EDGE,"E25"),sQuery(id+"F17.wireOp",EDGE,"E50.top"),sQuery(id+"F17.wireOp",EDGE,"E50.left"),sQuery(id+"F17.wireOp",EDGE,"E50.right")])],"capPos":1.0});
            var Q2;
            Q2=makeQuery(id+"F21.opLoft","MID_CAP_EDGE",EDGE,{"disambiguationData":[OSD([sQuery(id+"F6.wireOp",EDGE,"E26"),sQuery(id+"F6.wireOp",EDGE,"E27"),sQuery(id+"F6.wireOp",EDGE,"E28"),sQuery(id+"F20.wireOp",EDGE,"E53.bottom"),sQuery(id+"F20.wireOp",EDGE,"E53.left"),sQuery(id+"F20.wireOp",EDGE,"E53.right")])],"capPos":1.0});
            var Q3;
            Q3=makeQuery(id+"F18.opLoft","MID_CAP_EDGE",EDGE,{"disambiguationData":[OSD([sQuery(id+"F4.wireOp",EDGE,"E20.left"),sQuery(id+"F6.wireOp",EDGE,"E24"),sQuery(id+"F6.wireOp",EDGE,"E25"),sQuery(id+"F17.wireOp",EDGE,"E50.bottom"),sQuery(id+"F17.wireOp",EDGE,"E50.left"),sQuery(id+"F17.wireOp",EDGE,"E50.right")])],"capPos":1.0});
            var Q4;
            Q4=makeQuery(id+"F21.opLoft","MID_CAP_EDGE",EDGE,{"disambiguationData":[OSD([sQuery(id+"F12.wireOp",EDGE,"E35.0.2"),sQuery(id+"F12.wireOp",EDGE,"E35.0.3"),sQuery(id+"F12.wireOp",EDGE,"E36"),sQuery(id+"F12.wireOp",EDGE,"E37"),sQuery(id+"F19.wireOp",EDGE,"E52.top"),sQuery(id+"F19.wireOp",EDGE,"E52.left"),sQuery(id+"F19.wireOp",EDGE,"E52.right")])],"capPos":0.0});
            var Q5;
            Q5=makeQuery(id+"F18.opLoft","MID_CAP_EDGE",EDGE,{"disambiguationData":[OSD([sQuery(id+"F12.wireOp",EDGE,"E35.0.0"),sQuery(id+"F12.wireOp",EDGE,"E35.0.7"),sQuery(id+"F12.wireOp",EDGE,"E39"),sQuery(id+"F12.wireOp",EDGE,"E40"),sQuery(id+"F16.wireOp",EDGE,"E49.top"),sQuery(id+"F16.wireOp",EDGE,"E49.left"),sQuery(id+"F16.wireOp",EDGE,"E49.right")])],"capPos":0.0});
            var Q6;
            Q6=makeQuery(id+"F18.opLoft","MID_CAP_EDGE",EDGE,{"disambiguationData":[OSD([sQuery(id+"F6.wireOp",EDGE,"E24"),sQuery(id+"F6.wireOp",EDGE,"E25"),sQuery(id+"F6.wireOp",EDGE,"E28"),sQuery(id+"F17.wireOp",EDGE,"E51.top"),sQuery(id+"F17.wireOp",EDGE,"E50.left"),sQuery(id+"F17.wireOp",EDGE,"E51.right")])],"capPos":0.0});
            var Q7;
            Q7=makeQuery(id+"F18.opLoft","MID_CAP_EDGE",EDGE,{"disambiguationData":[OSD([sQuery(id+"F12.wireOp",EDGE,"E35.0.0"),sQuery(id+"F12.wireOp",EDGE,"E35.0.7"),sQuery(id+"F12.wireOp",EDGE,"E39"),sQuery(id+"F12.wireOp",EDGE,"E40"),sQuery(id+"F16.wireOp",EDGE,"E49.top"),sQuery(id+"F16.wireOp",EDGE,"E49.left"),sQuery(id+"F16.wireOp",EDGE,"E49.right")])],"capPos":1.0});
            fillet(context, id + "F27", {"entities" : qUnion([Q0, Q1, Q2, Q3, Q4, Q5, Q6, Q7]), "radius" : 5 * mm, "tangentPropagation" : true, "allowEdgeOverflow" : false});
        }
        {
            var Q0;
            Q0=makeQuery(id+"F13.boolean.opBoolean","MERGE",FACE,{"derivedFrom":[makeQuery(id+"F11.boolean.opBoolean","MERGE",FACE,{"derivedFrom":[makeQuery(id+"F7.boolean.opBoolean","MERGE",FACE,{"derivedFrom":[makeQuery(id+"F1.opExtrude","CAP_FACE",FACE,{"disambiguationData":[OSD([sQuery(id+"F0.wireOp",EDGE,"E1"),sQuery(id+"F0.wireOp",EDGE,"E2"),sQuery(id+"F0.wireOp",EDGE,"E3"),sQuery(id+"F0.wireOp",EDGE,"E4"),sQuery(id+"F0.wireOp",EDGE,"E5"),sQuery(id+"F0.wireOp",EDGE,"E6"),sQuery(id+"F0.wireOp",EDGE,"E7"),sQuery(id+"F0.wireOp",EDGE,"E8"),sQuery(id+"F0.wireOp",EDGE,"E9"),sQuery(id+"F0.wireOp",EDGE,"E10"),sQuery(id+"F0.wireOp",EDGE,"E11"),sQuery(id+"F0.wireOp",EDGE,"E12")])],"isStart":true}),makeQuery(id+"F7.opExtrude","SWEPT_FACE",FACE,{"disambiguationData":[OSD([sQuery(id+"F6.wireOp",EDGE,"E29")])]})]}),makeQuery(id+"F11.opExtrude","CAP_FACE",FACE,{"disambiguationData":[OSD([sQuery(id+"F10.wireOp",EDGE,"E33.0.0"),sQuery(id+"F10.wireOp",EDGE,"E33.0.1"),sQuery(id+"F10.wireOp",EDGE,"E33.0.2"),sQuery(id+"F10.wireOp",EDGE,"E33.0.3"),sQuery(id+"F10.wireOp",EDGE,"E33.0.13"),sQuery(id+"F10.wireOp",EDGE,"E33.0.14"),sQuery(id+"F10.wireOp",EDGE,"E33.0.15"),sQuery(id+"F10.wireOp",EDGE,"E34")])],"isStart":true})]}),makeQuery(id+"F13.opExtrude","CAP_FACE",FACE,{"disambiguationData":[OSD([sQuery(id+"F12.wireOp",EDGE,"E35.0.0"),sQuery(id+"F12.wireOp",EDGE,"E35.0.2"),sQuery(id+"F12.wireOp",EDGE,"E36"),sQuery(id+"F12.wireOp",EDGE,"E37"),sQuery(id+"F12.wireOp",EDGE,"E38"),sQuery(id+"F12.wireOp",EDGE,"E39"),sQuery(id+"F12.wireOp",EDGE,"E40"),sQuery(id+"F12.wireOp",EDGE,"E41"),sQuery(id+"F12.wireOp",EDGE,"E42"),sQuery(id+"F12.wireOp",EDGE,"E43")])],"isStart":true})]});
            var sketch = newSketch(context, id + "F28", { "sketchPlane" : qUnion([Q0])});
            skLineSegment(sketch, "E54.0", {"start": v(68.5, -1.6) * mm, "end": v(-2, -1.6) * mm});
            skLineSegment(sketch, "E55.0", {"start": v(68.5, -8.1) * mm, "end": v(68.5, -1.6) * mm});
            skLineSegment(sketch, "E56.0", {"start": v(13, -18.1) * mm, "end": v(68.5, -18.1) * mm});
            skLineSegment(sketch, "E57.0", {"start": v(-2, -1.6) * mm, "end": v(-2, -20.1) * mm});
            skSolve(sketch);
        }
        {
            var Q0;
            Q0=makeQuery(id+"F28.imprint","IMPRINT",FACE,{"disambiguationData":[TD([[makeQuery(id+"F28.imprint","IMPRINT",EDGE,{"derivedFrom":sQuery(id+"F28.wireOp",EDGE,"E54.0")}),1.0]])]});
            extrude(context, id + "F29", {"entities" : qUnion([Q0]), "operationType" : NewBodyOperationType.ADD, "oppositeDirection" : true, "depth" : 5 * mm, "offsetDistance" : 25 * mm});
        }
        {
            var Q0;
            Q0=makeQuery(id+"F3.boolean.opBoolean","COPY",EDGE,{"derivedFrom":makeQuery(id+"F3.opExtrude","SWEPT_EDGE",EDGE,{"disambiguationData":[OSD([sQuery(id+"F2.wireOp",EDGE,"E13.0.2"),sQuery(id+"F2.wireOp",EDGE,"E16.left")])]})});
            var Q1;
            Q1=makeQuery(id+"F3.boolean.opBoolean","COPY",EDGE,{"derivedFrom":makeQuery(id+"F3.opExtrude","SWEPT_EDGE",EDGE,{"disambiguationData":[OSD([sQuery(id+"F2.wireOp",EDGE,"E13.0.2"),sQuery(id+"F2.wireOp",EDGE,"E16.right")])]})});
            fillet(context, id + "F30", {"entities" : qUnion([Q0, Q1]), "radius" : 5 * mm, "tangentPropagation" : true, "allowEdgeOverflow" : false});
        }
        {
            var Q0;
            Q0=makeQuery(id+"F7.opExtrude","CAP_FACE",FACE,{"disambiguationData":[OSD([sQuery(id+"F6.wireOp",EDGE,"E24"),sQuery(id+"F6.wireOp",EDGE,"E25"),sQuery(id+"F6.wireOp",EDGE,"E26"),sQuery(id+"F6.wireOp",EDGE,"E27"),sQuery(id+"F6.wireOp",EDGE,"E28"),sQuery(id+"F6.wireOp",EDGE,"E29")])],"isStart":true});
            var sketch = newSketch(context, id + "F31", { "sketchPlane" : qUnion([Q0])});
            skLineSegment(sketch, "E58.0.0", {"start": v(-23.5, 13) * mm, "end": v(-22.5, 13) * mm});
            skLineSegment(sketch, "E58.0.1", {"start": v(-22.5, 13) * mm, "end": v(-22.5, 18) * mm});
            skLineSegment(sketch, "E58.0.2", {"start": v(-22.5, 18) * mm, "end": v(-25.02, 18) * mm});
            skArc(sketch, "E58.0.3", {"start": v(-25.02, 18) * mm, "mid": v(-23.89, 15.61) * mm, "end": v(-23.5, 13) * mm});
            skSolve(sketch);
        }
        {
            var Q0;
            Q0=makeQuery(id+"F31.imprint","IMPRINT",FACE,{"disambiguationData":[TD([[makeQuery(id+"F31.imprint","IMPRINT",EDGE,{"derivedFrom":sQuery(id+"F31.wireOp",EDGE,"E58.0.0")}),-1.0]])]});
            extrude(context, id + "F32", {"entities" : qUnion([Q0]), "operationType" : NewBodyOperationType.REMOVE, "endBound" : BoundingType.UP_TO_NEXT, "oppositeDirection" : true, "depth" : 25 * mm, "offsetDistance" : 25 * mm});
        }
    });
